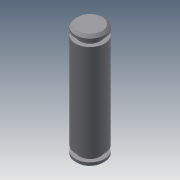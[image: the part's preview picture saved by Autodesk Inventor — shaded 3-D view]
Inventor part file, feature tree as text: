
AUTODESK INVENTOR PART (.ipt)
format: ipt  version: 2015 (Build 190159000, 159)  size: 102,912 bytes
history: native  units: mm
features: sketch x3, extrude x2, revolve x1, chamfer x1
ambient origin geometry x8: Origin, YZ Plane, XZ Plane, XY Plane, X Axis, Y Axis, Z Axis, Center Point
bodies: Solid1 (feature_tree)
feature tree (7):
  revolve  "Revolution1"  [1 undecoded]
  extrude  "Extrusion1"  Depth=1.0mm
  extrude  "Extrusion2"  Depth=2.0mm TaperAngle=0.0deg
  chamfer  "Chamfer1"  Distance=0.25mm
  sketch  "Sketch1"  dims[d12=19.5mm d13=1.0mm]
  sketch  "Sketch2"  dims[d14=0.85mm d16=1.0mm]
  sketch  "Sketch3"  dims[d17=90.0deg d18=0.25mm d19=0.0mm d20=0.25mm d21=0.0mm d22=0.5mm d23=2.0mm d24=45.0deg]
note: 1 required parameter value undecoded (feature->parameter linkage not recoverable at this tier; creation-order binding heuristic only, values carry confidence <= 0.55)
